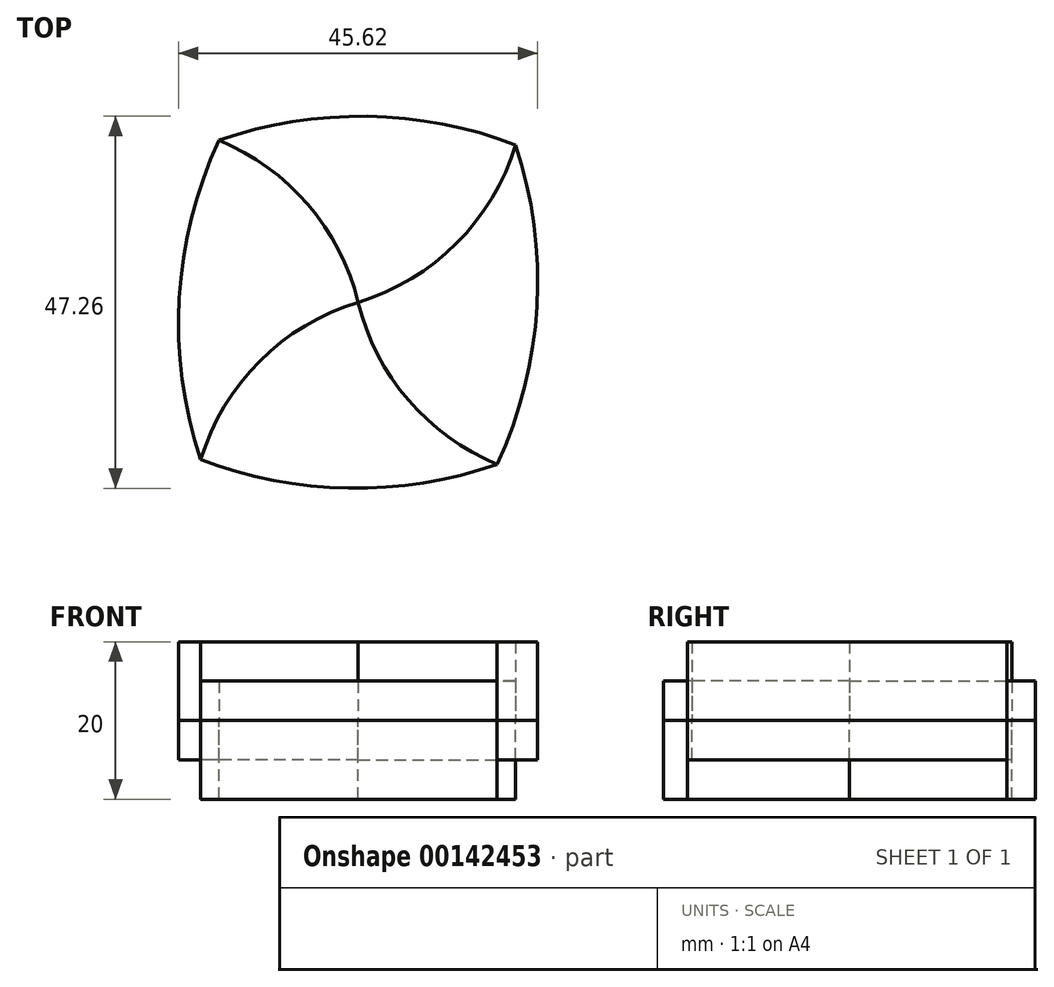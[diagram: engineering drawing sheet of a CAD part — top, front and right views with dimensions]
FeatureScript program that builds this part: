
annotation { "Feature Type Name" : "Feature", "Feature Type Description" : "" }
export const myFeature = defineFeature(function(context is Context, id is Id, definition is map)
    precondition{}
    {
        {
            var Q0;
            Q0=qCreatedBy(makeId("Top.planeOp"),FACE);
            var sketch = newSketch(context, id + "F0", { "sketchPlane" : qUnion([Q0])});
            skPoint(sketch, "E0.middle", {"position": v(0, 0) * mm});
            skArc(sketch, "E1", {"start": v(0, 0) * mm, "mid": v(-6.38, 12.4) * mm, "end": v(-17.67, 20.6) * mm});
            skArc(sketch, "E2", {"start": v(0, 0) * mm, "mid": v(12.5, 7.5) * mm, "end": v(20, 20) * mm});
            skArc(sketch, "E3", {"start": v(0, 0) * mm, "mid": v(6.38, -12.4) * mm, "end": v(17.67, -20.6) * mm});
            skArc(sketch, "E4", {"start": v(0, 0) * mm, "mid": v(-12.5, -7.5) * mm, "end": v(-20, -20) * mm});
            skArc(sketch, "E5", {"start": v(20, 20) * mm, "mid": v(1.22, 23.62) * mm, "end": v(-17.67, 20.6) * mm});
            skArc(sketch, "E6", {"start": v(-17.67, 20.6) * mm, "mid": v(-22.72, 0.52) * mm, "end": v(-20, -20) * mm});
            skArc(sketch, "E7", {"start": v(17.67, -20.6) * mm, "mid": v(22.72, -0.52) * mm, "end": v(20, 20) * mm});
            skArc(sketch, "E8", {"start": v(-20, -20) * mm, "mid": v(-1.22, -23.62) * mm, "end": v(17.67, -20.6) * mm});
            skSolve(sketch);
        }
        {
            var Q0;
            Q0=makeQuery(id+"F0.imprint","IMPRINT",FACE,{"disambiguationData":[TD([[makeQuery(id+"F0.imprint","IMPRINT",EDGE,{"derivedFrom":sQuery(id+"F0.wireOp",EDGE,"E1")}),1.0]])]});
            var Q1;
            Q1=makeQuery(id+"F0.imprint","IMPRINT",FACE,{"disambiguationData":[TD([[makeQuery(id+"F0.imprint","IMPRINT",EDGE,{"derivedFrom":sQuery(id+"F0.wireOp",EDGE,"E2")}),-1.0]])]});
            extrude(context, id + "F1", {"entities" : qUnion([Q0, Q1]), "depth" : 10 * mm});
        }
        {
            var Q0;
            Q0=makeQuery(id+"F1.opExtrude","CAP_FACE",FACE,{"disambiguationData":[OSD([sQuery(id+"F0.wireOp",EDGE,"E1"),sQuery(id+"F0.wireOp",EDGE,"E4"),sQuery(id+"F0.wireOp",EDGE,"E6")])],"isStart":true});
            var Q1;
            Q1=makeQuery(id+"F1.opExtrude","CAP_FACE",FACE,{"disambiguationData":[OSD([sQuery(id+"F0.wireOp",EDGE,"E2"),sQuery(id+"F0.wireOp",EDGE,"E3"),sQuery(id+"F0.wireOp",EDGE,"E7")])],"isStart":true});
            extrude(context, id + "F2", {"entities" : qUnion([Q0, Q1]), "depth" : 5 * mm});
        }
        {
            var Q0;
            Q0=makeQuery(id+"F0.imprint","IMPRINT",FACE,{"disambiguationData":[TD([[makeQuery(id+"F0.imprint","IMPRINT",EDGE,{"derivedFrom":sQuery(id+"F0.wireOp",EDGE,"E1")}),-1.0]])]});
            var Q1;
            Q1=makeQuery(id+"F0.imprint","IMPRINT",FACE,{"disambiguationData":[TD([[makeQuery(id+"F0.imprint","IMPRINT",EDGE,{"derivedFrom":sQuery(id+"F0.wireOp",EDGE,"E3")}),-1.0]])]});
            extrude(context, id + "F3", {"entities" : qUnion([Q0, Q1]), "oppositeDirection" : true, "depth" : 10 * mm});
        }
        {
            var Q0;
            Q0=makeQuery(id+"F0.imprint","IMPRINT",FACE,{"disambiguationData":[TD([[makeQuery(id+"F0.imprint","IMPRINT",EDGE,{"derivedFrom":sQuery(id+"F0.wireOp",EDGE,"E1")}),-1.0]])]});
            var Q1;
            Q1=makeQuery(id+"F0.imprint","IMPRINT",FACE,{"disambiguationData":[TD([[makeQuery(id+"F0.imprint","IMPRINT",EDGE,{"derivedFrom":sQuery(id+"F0.wireOp",EDGE,"E3")}),-1.0]])]});
            extrude(context, id + "F4", {"entities" : qUnion([Q0, Q1]), "depth" : 5 * mm});
        }
    });
